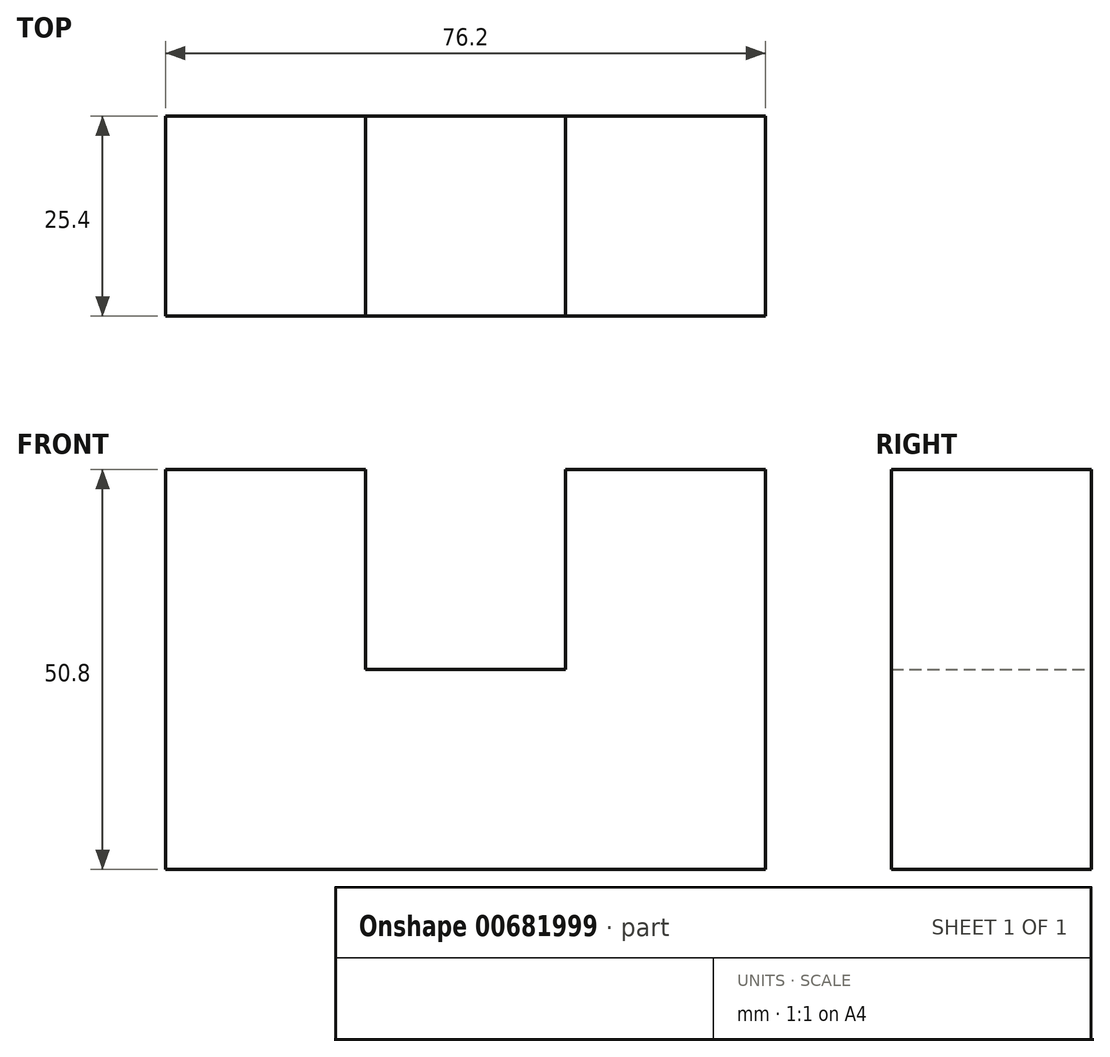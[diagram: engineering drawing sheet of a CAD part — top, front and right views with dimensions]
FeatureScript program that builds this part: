
annotation { "Feature Type Name" : "Feature", "Feature Type Description" : "" }
export const myFeature = defineFeature(function(context is Context, id is Id, definition is map)
    precondition{}
    {
        {
            var Q0;
            Q0=qCreatedBy(makeId("Front.planeOp"),FACE);
            var sketch = newSketch(context, id + "F0", { "sketchPlane" : qUnion([Q0])});
            skLineSegment(sketch, "E0", {"start": v(0, 0) * mm, "end": v(-76.2, 0) * mm});
            skLineSegment(sketch, "E1", {"start": v(-76.2, 0) * mm, "end": v(-76.2, 50.8) * mm});
            skLineSegment(sketch, "E2", {"start": v(-76.2, 50.8) * mm, "end": v(-50.8, 50.8) * mm});
            skLineSegment(sketch, "E3", {"start": v(-50.8, 50.8) * mm, "end": v(-50.8, 25.4) * mm});
            skLineSegment(sketch, "E4", {"start": v(-50.8, 25.4) * mm, "end": v(-25.4, 25.4) * mm});
            skLineSegment(sketch, "E5", {"start": v(-25.4, 25.4) * mm, "end": v(-25.4, 50.8) * mm});
            skLineSegment(sketch, "E6", {"start": v(-25.4, 50.8) * mm, "end": v(0, 50.8) * mm});
            skLineSegment(sketch, "E7", {"start": v(0, 50.8) * mm, "end": v(0, 0) * mm});
            skSolve(sketch);
        }
        {
            var Q0;
            Q0=makeQuery(id+"F0.imprint","IMPRINT",FACE,{"disambiguationData":[TD([[makeQuery(id+"F0.imprint","IMPRINT",EDGE,{"derivedFrom":sQuery(id+"F0.wireOp",EDGE,"E0")}),-1.0]])]});
            extrude(context, id + "F1", {"entities" : qUnion([Q0]), "depth" : 25.4 * mm, "offsetDistance" : 25.4 * mm});
        }
    });
